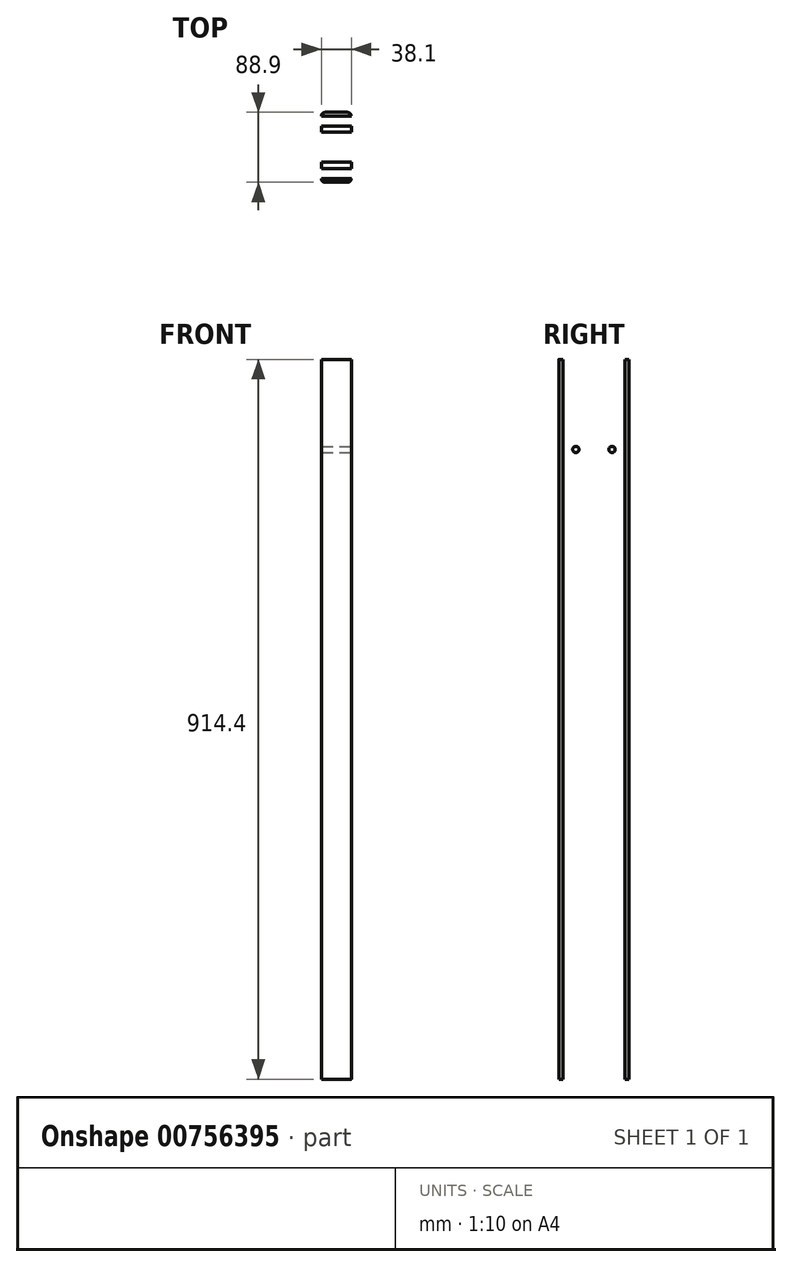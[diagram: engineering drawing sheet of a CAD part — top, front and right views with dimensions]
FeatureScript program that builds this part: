
annotation { "Feature Type Name" : "Feature", "Feature Type Description" : "" }
export const myFeature = defineFeature(function(context is Context, id is Id, definition is map)
    precondition{}
    {
        {
            var Q0;
            Q0=qCreatedBy(makeId("Top.planeOp"),FACE);
            var sketch = newSketch(context, id + "F0", { "sketchPlane" : qUnion([Q0])});
            skLineSegment(sketch, "E0.bottom", {"start": v(5, 0) * mm, "end": v(33.1, 0) * mm});
            skLineSegment(sketch, "E0.top", {"start": v(5, 88.9) * mm, "end": v(33.1, 88.9) * mm});
            skLineSegment(sketch, "E0.left", {"start": v(0, 5) * mm, "end": v(0, 83.9) * mm});
            skLineSegment(sketch, "E0.right", {"start": v(38.1, 5) * mm, "end": v(38.1, 83.9) * mm});
            skPoint(sketch, "E1.visualSharp", {"position": v(0, 88.9) * mm});
            skArc(sketch, "E1.filletArc", {"start": v(5, 88.9) * mm, "mid": v(1.46, 87.44) * mm, "end": v(0, 83.9) * mm});
            skPoint(sketch, "E2.visualSharp", {"position": v(38.1, 88.9) * mm});
            skArc(sketch, "E2.filletArc", {"start": v(38.1, 83.9) * mm, "mid": v(36.64, 87.44) * mm, "end": v(33.1, 88.9) * mm});
            skPoint(sketch, "E3.visualSharp", {"position": v(38.1, 0) * mm});
            skArc(sketch, "E3.filletArc", {"start": v(33.1, 0) * mm, "mid": v(36.64, 1.46) * mm, "end": v(38.1, 5) * mm});
            skPoint(sketch, "E4.visualSharp", {"position": v(0, 0) * mm});
            skArc(sketch, "E4.filletArc", {"start": v(0, 5) * mm, "mid": v(1.46, 1.46) * mm, "end": v(5, 0) * mm});
            skSolve(sketch);
        }
        {
            var Q0;
            Q0=makeQuery(id+"F0.imprint","IMPRINT",FACE,{"disambiguationData":[TD([[makeQuery(id+"F0.imprint","IMPRINT",EDGE,{"derivedFrom":sQuery(id+"F0.wireOp",EDGE,"E0.bottom")}),1.0]])]});
            extrude(context, id + "F1", {"entities" : qUnion([Q0]), "depth" : 914.4 * mm, "offsetDistance" : 25.4 * mm});
        }
        {
            var Q0;
            Q0=makeQuery(id+"F1.opExtrude","SWEPT_FACE",FACE,{"disambiguationData":[OSD([sQuery(id+"F0.wireOp",EDGE,"E0.right")])]});
            var sketch = newSketch(context, id + "F2", { "sketchPlane" : qUnion([Q0])});
            skLineSegment(sketch, "E5", {"start": v(21.43, 114.3) * mm, "end": v(67.47, 114.3) * mm, "construction": true});
            skCircle(sketch, "E6", {"center": v(21.43, 114.3) * mm, "radius": 3.97 * mm});
            skCircle(sketch, "E7", {"center": v(67.47, 114.3) * mm, "radius": 3.97 * mm});
            skPoint(sketch, "E8", {"position": v(44.45, 114.3) * mm});
            skLineSegment(sketch, "E9", {"start": v(83.9, 457.2) * mm, "end": v(5, 457.2) * mm, "construction": true});
            skCircle(sketch, "E10.MirrorC", {"center": v(21.43, 800.1) * mm, "radius": 3.97 * mm});
            skCircle(sketch, "E11.MirrorC", {"center": v(67.47, 800.1) * mm, "radius": 3.97 * mm});
            skLineSegment(sketch, "E12", {"start": v(44.45, 114.3) * mm, "end": v(44.45, 800.1) * mm, "construction": true});
            skPoint(sketch, "E13", {"position": v(44.45, 457.2) * mm});
            skSolve(sketch);
        }
        {
            var Q0;
            Q0=makeQuery(id+"F2.imprint","IMPRINT",FACE,{"disambiguationData":[TD([[makeQuery(id+"F2.imprint","IMPRINT",EDGE,{"derivedFrom":sQuery(id+"F2.wireOp",EDGE,"E6")}),1.0]])]});
            var Q1;
            Q1=makeQuery(id+"F2.imprint","IMPRINT",FACE,{"disambiguationData":[TD([[makeQuery(id+"F2.imprint","IMPRINT",EDGE,{"derivedFrom":sQuery(id+"F2.wireOp",EDGE,"E7")}),1.0]])]});
            var Q2;
            Q2=makeQuery(id+"F2.imprint","IMPRINT",FACE,{"disambiguationData":[TD([[makeQuery(id+"F2.imprint","IMPRINT",EDGE,{"derivedFrom":sQuery(id+"F2.wireOp",EDGE,"E10.MirrorC")}),-1.0]])]});
            var Q3;
            Q3=makeQuery(id+"F2.imprint","IMPRINT",FACE,{"disambiguationData":[TD([[makeQuery(id+"F2.imprint","IMPRINT",EDGE,{"derivedFrom":sQuery(id+"F2.wireOp",EDGE,"E11.MirrorC")}),-1.0]])]});
            extrude(context, id + "F3", {"entities" : qUnion([Q0, Q1, Q2, Q3]), "operationType" : NewBodyOperationType.REMOVE, "endBound" : BoundingType.THROUGH_ALL, "oppositeDirection" : true, "depth" : 25 * mm, "offsetDistance" : 25 * mm});
        }
    });
